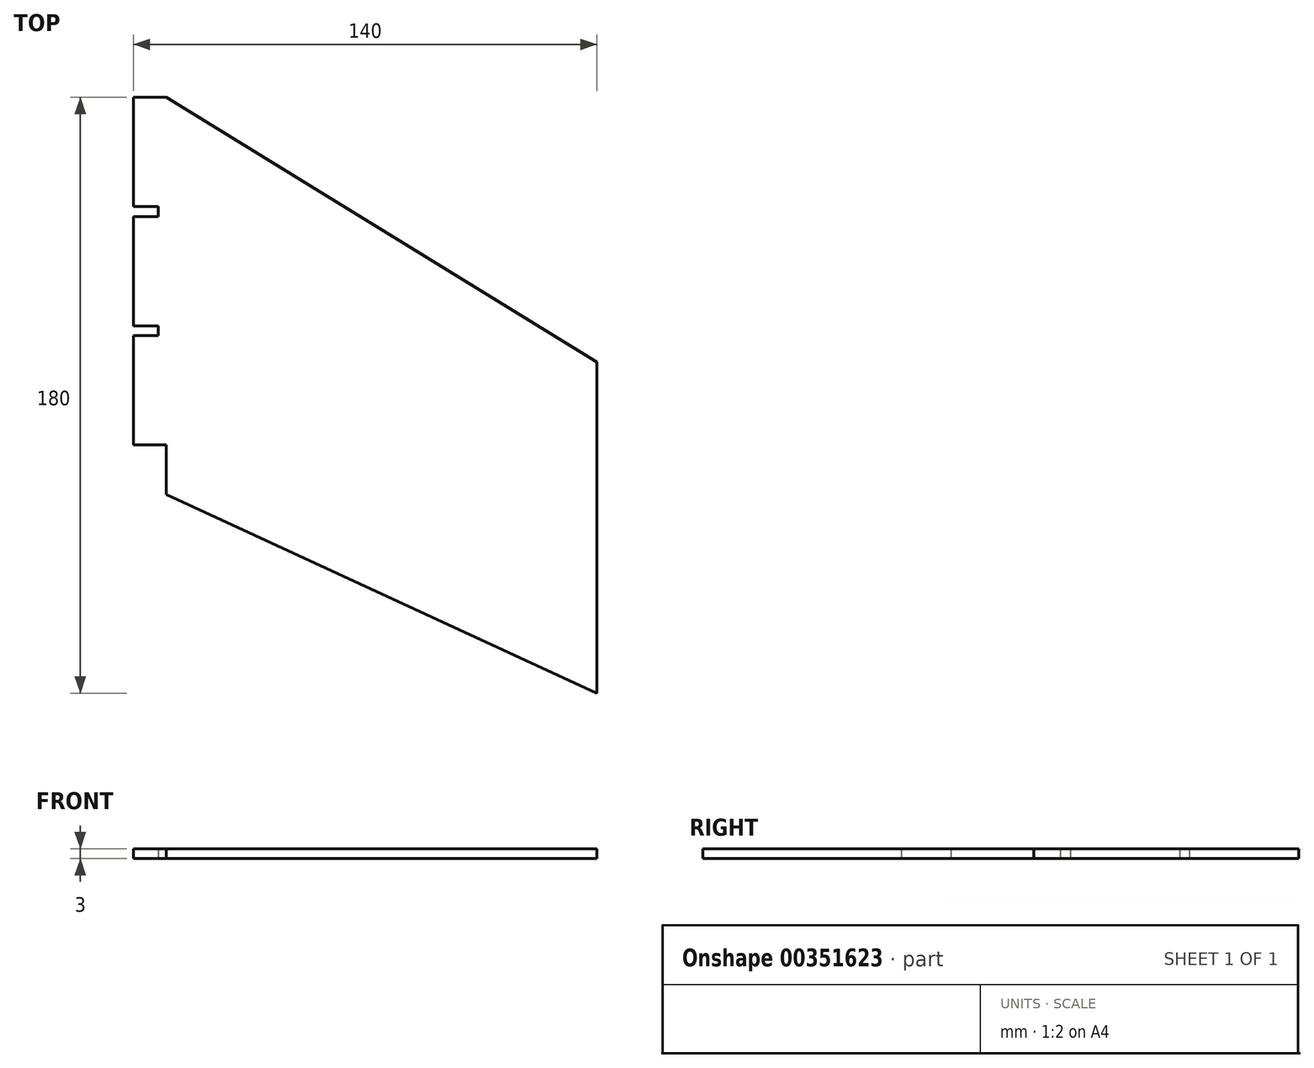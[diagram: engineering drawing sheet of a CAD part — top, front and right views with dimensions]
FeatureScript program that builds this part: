
annotation { "Feature Type Name" : "Feature", "Feature Type Description" : "" }
export const myFeature = defineFeature(function(context is Context, id is Id, definition is map)
    precondition{}
    {
        {
            var Q0;
            Q0=qCreatedBy(makeId("Top.planeOp"),FACE);
            var sketch = newSketch(context, id + "F0", { "sketchPlane" : qUnion([Q0])});
            skLineSegment(sketch, "E0", {"start": v(0, 0) * mm, "end": v(0, 15) * mm});
            skLineSegment(sketch, "E1", {"start": v(0, 120) * mm, "end": v(130, 40) * mm});
            skLineSegment(sketch, "E2", {"start": v(130, 40) * mm, "end": v(130, -60) * mm});
            skLineSegment(sketch, "E3", {"start": v(0, 0) * mm, "end": v(130, -60) * mm});
            skLineSegment(sketch, "E4.bottom", {"start": v(0, 120) * mm, "end": v(-10, 120) * mm});
            skLineSegment(sketch, "E4.left", {"start": v(0, 15) * mm, "end": v(0, 0) * mm});
            skLineSegment(sketch, "E4.right", {"start": v(-10, 120) * mm, "end": v(-10, 87) * mm});
            skLineSegment(sketch, "E5.top", {"start": v(-10, 15) * mm, "end": v(0, 15) * mm});
            skPoint(sketch, "E6.orphan", {"position": v(-10, 0) * mm});
            skLineSegment(sketch, "E7", {"start": v(-10, 87) * mm, "end": v(-2.5, 87) * mm});
            skLineSegment(sketch, "E8", {"start": v(-10, 84) * mm, "end": v(-2.5, 84) * mm});
            skLineSegment(sketch, "E9", {"start": v(-2.5, 87) * mm, "end": v(-2.5, 84) * mm});
            skLineSegment(sketch, "E10.trimOffspring", {"start": v(-10, 84) * mm, "end": v(-10, 51) * mm});
            skLineSegment(sketch, "E11.bottom", {"start": v(-10, 51) * mm, "end": v(-2.5, 51) * mm});
            skLineSegment(sketch, "E11.top", {"start": v(-10, 48) * mm, "end": v(-2.5, 48) * mm});
            skLineSegment(sketch, "E11.right", {"start": v(-2.5, 51) * mm, "end": v(-2.5, 48) * mm});
            skLineSegment(sketch, "E12.trimOffspring", {"start": v(-10, 48) * mm, "end": v(-10, 15) * mm});
            skSolve(sketch);
        }
        {
            var Q0;
            Q0=makeQuery(id+"F0.imprint","IMPRINT",FACE,{"disambiguationData":[TD([[makeQuery(id+"F0.imprint","IMPRINT",EDGE,{"derivedFrom":sQuery(id+"F0.wireOp",EDGE,"E1")}),-1.0]])]});
            extrude(context, id + "F1", {"entities" : qUnion([Q0]), "depth" : 3 * mm});
        }
    });
